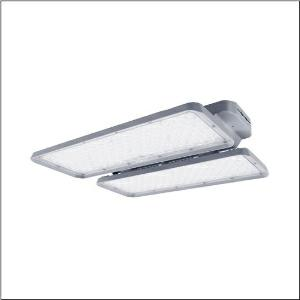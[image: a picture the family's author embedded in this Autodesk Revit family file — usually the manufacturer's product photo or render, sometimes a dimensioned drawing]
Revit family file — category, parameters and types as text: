
# Revit family: highbay_21-l_51hk42db4mca
name_source: partatom
category: Lighting Fixtures
units: mm (PartAtom-declared; Revit-internal decimal feet)

## family parameters
Cut with Voids When Loaded = No
Host = Face
Light Source = No
Part Type = Normal
Room Calculation Point = No
Round Connector Dimension = Use Diameter
Shared = No

## types (1)
- Highbay 21-L (1 x LED, 26500 lm, 147 W, 4000K)
    Apparent Load = 147 VA
    CIE Flux Codes = 75 96 99 100 100
    Color Rendering = 80
    Color Temperature = 4000K
    Default Elevation = 1800 mm
    Description = Highbay 21-L, LED high bay luminaire, primary light control with lens, of PC, light emission: direct distribution, primary light characteristic: symmetric, installation type: suspended mounting, surface-mounted, LED, rated luminous flux: 26.500lm, luminous efficacy: 178lm/W, light colour: 840, colour temperature: 4000K, with terminal, 5-pole, max. 2.5mm², mains connection: 220..240V, AC, 50Hz, rated input power: 147W, housing, of diecast aluminium, coated, grey, length: 471mm, width: 390mm, height: 87mm, protection rating (complete): IP66, insulation class (complete): insulation class I (protective earthing), certification: CE, ENEC, UKCA, protection symbol: D, impact resistance: IK08, permissible operating ambient temperature: -30..+60°C, corresponds to IFS (International Featured Standards) requirements for safety and quality in the food industry, LABS conformity tested according to VDMA 24364:2018-05, packaging unit: 1 piece
    Height = 89 mm
    Lamp = 1 x LED
    Lamp Light Flux = 26500 lm
    Lamp Power = 147 W
    Lamp count = 1
    Length = 471 mm
    Luminous efficacy = 180 lm/W
    Manufacturer = Siteco
    ModVariant = No
    Model = 51HK42DB4MCA
    Mounting Place = Ceiling
    Mounting Type = Pendant
    Number of Poles = 1
    OnlyDefault = Yes
    Power Factor = 1
    Product Name = Highbay 21-L
    Product group = LED high bay luminaire
    ProductGroupID = 903
    Protection Class = Protection class I
    Protection Degree = IP 66
    RLX_Detail_Level = 1
    RLX_Emergency_Light_Flux = 0 lm
    RLX_Emergency_Type = 0
    RLX_Emergency_Type_DB = No
    RlxData = <blob elided: 25969 chars, md5=a9bbe584>
    Socket = socket
    Standby Power = 0 W
    System Light Flux = 26500 lm
    System Power = 147 W
    Type Comments = Product without accessories
    Type Image = l_1276530.jpg
    URL = http://relux.com
    VarID = ---
    Voltage = 0 V
    Weight = 0.00 kg
    Width = 390 mm

## geometry (parser evidence)
native form markers: Blend x4, Sweep x9
no freeform markers — native parametric forms only
